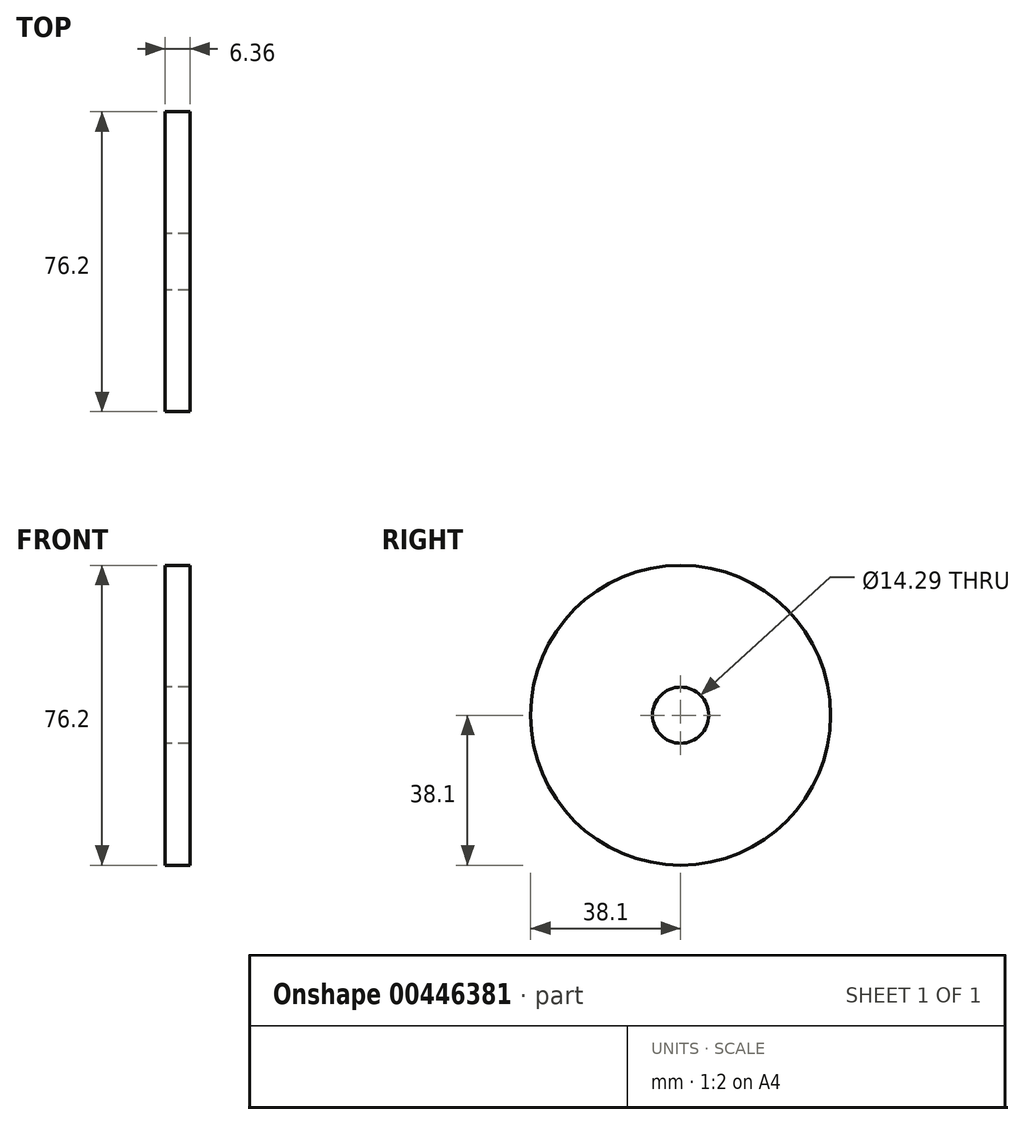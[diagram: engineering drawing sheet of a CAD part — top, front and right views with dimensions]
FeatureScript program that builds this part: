
annotation { "Feature Type Name" : "Feature", "Feature Type Description" : "" }
export const myFeature = defineFeature(function(context is Context, id is Id, definition is map)
    precondition{}
    {
        {
            var Q0;
            Q0=qCreatedBy(makeId("Right.planeOp"),FACE);
            var sketch = newSketch(context, id + "F0", { "sketchPlane" : qUnion([Q0])});
            skCircle(sketch, "E0", {"center": v(0, 0) * mm, "radius": 38.1 * mm});
            skCircle(sketch, "E1", {"center": v(0, 0) * mm, "radius": 7.14 * mm});
            skSolve(sketch);
        }
        {
            var Q0;
            Q0 = qSketchRegion(id + "F0", true);
            extrude(context, id + "F1", {"entities" : qUnion([Q0]), "depth" : 6.35 * mm, "offsetDistance" : 25.4 * mm, "symmetric" : true});
        }
    });
